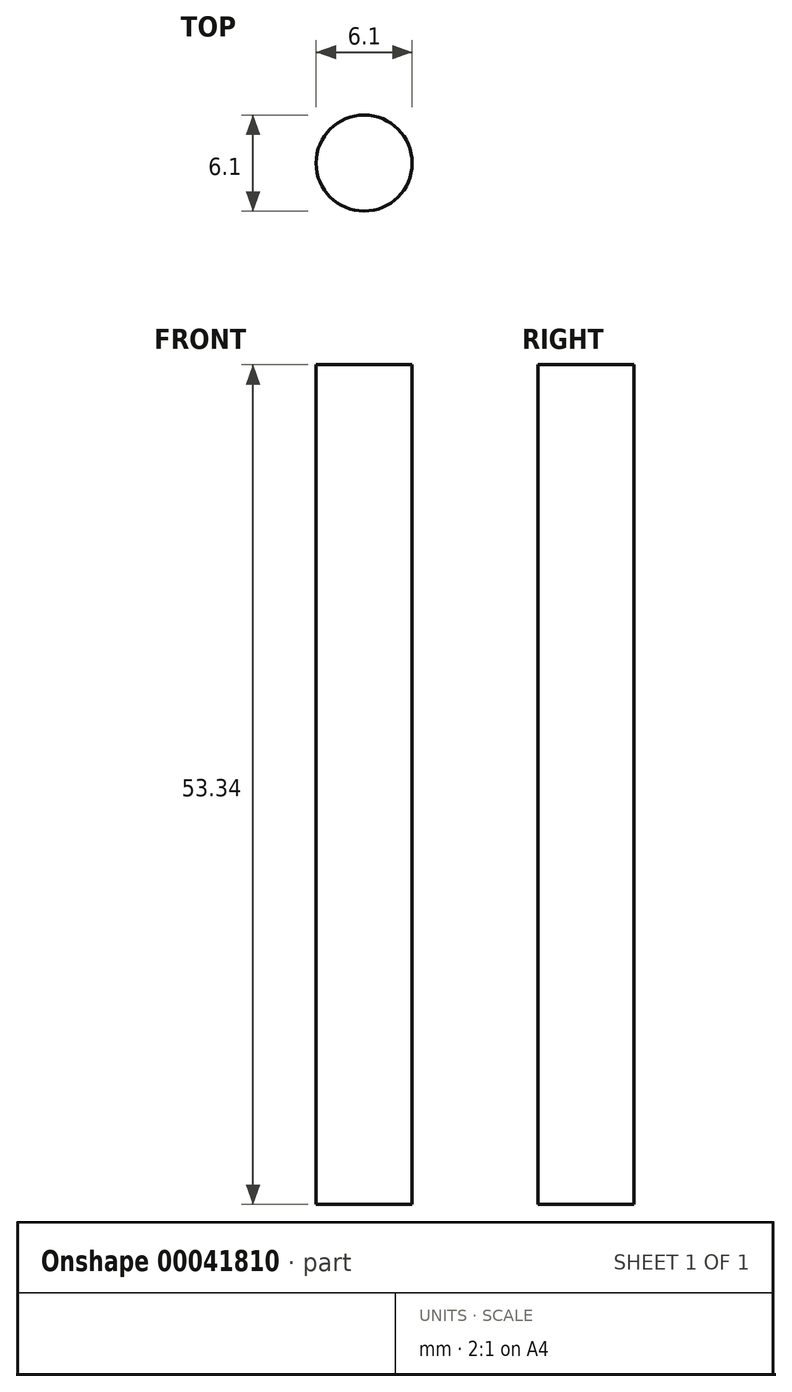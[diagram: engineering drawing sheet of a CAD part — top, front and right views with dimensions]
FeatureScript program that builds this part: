
annotation { "Feature Type Name" : "Feature", "Feature Type Description" : "" }
export const myFeature = defineFeature(function(context is Context, id is Id, definition is map)
    precondition{}
    {
        {
            var Q0;
            Q0=qCreatedBy(makeId("Top.planeOp"),FACE);
            var sketch = newSketch(context, id + "F0", { "sketchPlane" : qUnion([Q0])});
            skCircle(sketch, "E0", {"center": v(-25.4, 38.1) * mm, "radius": 3.05 * mm});
            skCircle(sketch, "E1.MirrorC", {"center": v(25.4, 38.1) * mm, "radius": 3.05 * mm});
            skSolve(sketch);
        }
        {
            var Q0;
            Q0=makeQuery(id+"F0.imprint","IMPRINT",FACE,{"disambiguationData":[TD([[makeQuery(id+"F0.imprint","IMPRINT",EDGE,{"derivedFrom":sQuery(id+"F0.wireOp",EDGE,"E0")}),1.0]])]});
            var Q1;
            Q1=makeQuery(id+"F0.imprint","IMPRINT",FACE,{"disambiguationData":[TD([[makeQuery(id+"F0.imprint","IMPRINT",EDGE,{"derivedFrom":sQuery(id+"F0.wireOp",EDGE,"E1.MirrorC")}),-1.0]])]});
            extrude(context, id + "F1", {"entities" : qUnion([Q0, Q1]), "depth" : 53.34 * mm});
        }
    });
